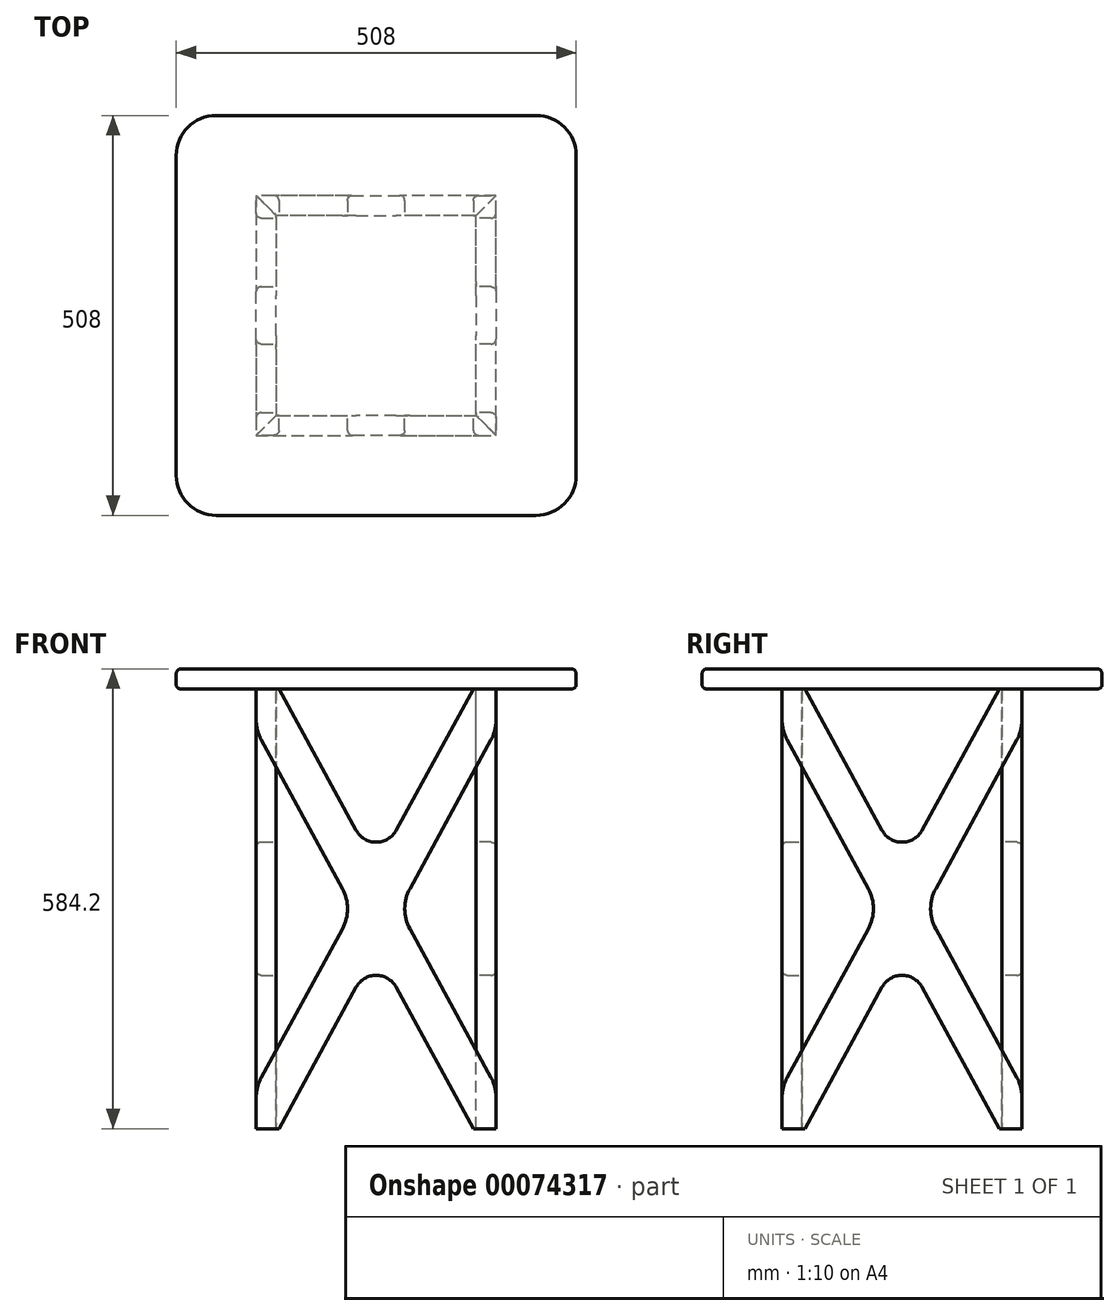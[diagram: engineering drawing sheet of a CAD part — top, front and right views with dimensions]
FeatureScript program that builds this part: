
annotation { "Feature Type Name" : "Feature", "Feature Type Description" : "" }
export const myFeature = defineFeature(function(context is Context, id is Id, definition is map)
    precondition{}
    {
        {
            var Q0;
            Q0=qCreatedBy(makeId("Right.planeOp"),FACE);
            var sketch = newSketch(context, id + "F0", { "sketchPlane" : qUnion([Q0])});
            skLineSegment(sketch, "E0.bottom", {"start": v(-152.4, 558.8) * mm, "end": v(152.4, 558.8) * mm, "construction": true});
            skLineSegment(sketch, "E0.top", {"start": v(-152.4, 0) * mm, "end": v(152.4, 0) * mm, "construction": true});
            skLineSegment(sketch, "E0.left", {"start": v(-152.4, 558.8) * mm, "end": v(-152.4, 505.76) * mm});
            skLineSegment(sketch, "E0.right", {"start": v(152.4, 558.8) * mm, "end": v(152.4, 505.76) * mm});
            skLineSegment(sketch, "E1", {"start": v(-152.4, 0) * mm, "end": v(152.4, 558.8) * mm, "construction": true});
            skLineSegment(sketch, "E2", {"start": v(-152.4, 558.8) * mm, "end": v(152.4, 0) * mm, "construction": true});
            skLineSegment(sketch, "E3.0", {"start": v(-152.4, 505.76) * mm, "end": v(-42.79, 304.8) * mm});
            skLineSegment(sketch, "E4.0", {"start": v(-123.47, 558.8) * mm, "end": v(-25.4, 379.01) * mm});
            skLineSegment(sketch, "E5.0", {"start": v(-123.47, 0) * mm, "end": v(-25.4, 179.79) * mm});
            skLineSegment(sketch, "E6.0", {"start": v(-152.4, 53.04) * mm, "end": v(-42.79, 254) * mm});
            skLineSegment(sketch, "E7.trimOffspring", {"start": v(25.4, 379.01) * mm, "end": v(123.47, 558.8) * mm});
            skLineSegment(sketch, "E8.trimOffspring", {"start": v(25.4, 179.79) * mm, "end": v(123.47, 0) * mm});
            skLineSegment(sketch, "E9.trimOffspring", {"start": v(42.79, 254) * mm, "end": v(152.4, 53.04) * mm});
            skPoint(sketch, "E10.visualSharp", {"position": v(0, 332.44) * mm});
            skArc(sketch, "E10.filletArc", {"start": v(-25.4, 379.01) * mm, "mid": v(0, 363.93) * mm, "end": v(25.4, 379.01) * mm});
            skPoint(sketch, "E11.visualSharp", {"position": v(-28.93, 279.4) * mm});
            skArc(sketch, "E11.filletArc", {"start": v(-42.79, 254) * mm, "mid": v(-36.31, 279.4) * mm, "end": v(-42.79, 304.8) * mm});
            skLineSegment(sketch, "E12.trimOffspring", {"start": v(42.79, 304.8) * mm, "end": v(152.4, 505.76) * mm});
            skPoint(sketch, "E13.visualSharp", {"position": v(0, 226.36) * mm});
            skArc(sketch, "E13.filletArc", {"start": v(25.4, 179.79) * mm, "mid": v(0, 194.87) * mm, "end": v(-25.4, 179.79) * mm});
            skPoint(sketch, "E14.visualSharp", {"position": v(28.93, 279.4) * mm});
            skArc(sketch, "E14.filletArc", {"start": v(42.79, 304.8) * mm, "mid": v(36.31, 279.4) * mm, "end": v(42.79, 254) * mm});
            skLineSegment(sketch, "E15", {"start": v(-123.47, 558.8) * mm, "end": v(-152.4, 558.8) * mm});
            skLineSegment(sketch, "E16", {"start": v(123.47, 558.8) * mm, "end": v(152.4, 558.8) * mm});
            skLineSegment(sketch, "E17", {"start": v(-152.4, 0) * mm, "end": v(-123.47, 0) * mm});
            skLineSegment(sketch, "E18.trimOffspring", {"start": v(123.47, 0) * mm, "end": v(152.4, 0) * mm});
            skLineSegment(sketch, "E19", {"start": v(0, 0) * mm, "end": v(0, 558.8) * mm, "construction": true});
            skPoint(sketch, "E20", {"position": v(0, 279.4) * mm});
            skLineSegment(sketch, "E21.trimOffspring", {"start": v(-152.4, 53.04) * mm, "end": v(-152.4, 0) * mm});
            skLineSegment(sketch, "E22.trimOffspring", {"start": v(152.4, 53.04) * mm, "end": v(152.4, 0) * mm});
            skSolve(sketch);
        }
        {
            var Q0;
            Q0=makeQuery(id+"F0.imprint","IMPRINT",FACE,{"disambiguationData":[TD([[makeQuery(id+"F0.imprint","IMPRINT",EDGE,{"derivedFrom":sQuery(id+"F0.wireOp",EDGE,"E3.0")}),1.0]])]});
            extrude(context, id + "F1", {"entities" : qUnion([Q0]), "depth" : 152.4 * mm, "offsetDistance" : 25.4 * mm, "hasSecondDirection" : true, "secondDirectionOppositeDirection" : false, "secondDirectionDepth" : 127 * mm});
        }
        {
            var Q0;
            Q0=makeQuery(id+"F1.opExtrude","CAP_EDGE",EDGE,{"disambiguationData":[OSD([sQuery(id+"F0.wireOp",EDGE,"E0.right")])],"isStart":true});
            var Q1;
            Q1=makeQuery(id+"F1.opExtrude","CAP_EDGE",EDGE,{"disambiguationData":[OSD([sQuery(id+"F0.wireOp",EDGE,"E22.trimOffspring")])],"isStart":true});
            var Q2;
            Q2=makeQuery(id+"F1.opExtrude","CAP_EDGE",EDGE,{"disambiguationData":[OSD([sQuery(id+"F0.wireOp",EDGE,"E0.left")])],"isStart":true});
            var Q3;
            Q3=makeQuery(id+"F1.opExtrude","CAP_EDGE",EDGE,{"disambiguationData":[OSD([sQuery(id+"F0.wireOp",EDGE,"E21.trimOffspring")])],"isStart":true});
            chamfer(context, id + "F2", {"entities" : qUnion([Q0, Q1, Q2, Q3]), "width" : 25.4 * mm, "tangentPropagation" : true});
        }
        {
            var Q0;
            Q0=makeQuery(id+"F1.opExtrude","CAP_EDGE",EDGE,{"disambiguationData":[OSD([sQuery(id+"F0.wireOp",EDGE,"E3.0")])],"isStart":false});
            var Q1;
            Q1=makeQuery(id+"F1.opExtrude","CAP_EDGE",EDGE,{"disambiguationData":[OSD([sQuery(id+"F0.wireOp",EDGE,"E4.0")])],"isStart":false});
            var Q2;
            Q2=makeQuery(id+"F1.opExtrude","CAP_EDGE",EDGE,{"disambiguationData":[OSD([sQuery(id+"F0.wireOp",EDGE,"E12.trimOffspring")])],"isStart":false});
            var Q3;
            Q3=makeQuery(id+"F1.opExtrude","CAP_EDGE",EDGE,{"disambiguationData":[OSD([sQuery(id+"F0.wireOp",EDGE,"E8.trimOffspring")])],"isStart":false});
            fillet(context, id + "F3", {"entities" : qUnion([Q0, Q1, Q2, Q3]), "tangentPropagation" : true, "radius" : 6.35 * mm, "defaultsChanged" : true, "vertexSettings" : [], "allowEdgeOverflow" : false});
        }
        {
            var Q0;
            Q0=makeQuery(id+"F1.opExtrude","SWEPT_BODY",BODY,{"disambiguationData":[OSD([sQuery(id+"F0.wireOp",EDGE,"E3.0"),sQuery(id+"F0.wireOp",EDGE,"E4.0"),sQuery(id+"F0.wireOp",EDGE,"E5.0"),sQuery(id+"F0.wireOp",EDGE,"E6.0"),sQuery(id+"F0.wireOp",EDGE,"E7.trimOffspring"),sQuery(id+"F0.wireOp",EDGE,"E8.trimOffspring"),sQuery(id+"F0.wireOp",EDGE,"E9.trimOffspring"),sQuery(id+"F0.wireOp",EDGE,"E10.filletArc"),sQuery(id+"F0.wireOp",EDGE,"E11.filletArc"),sQuery(id+"F0.wireOp",EDGE,"E12.trimOffspring"),sQuery(id+"F0.wireOp",EDGE,"E13.filletArc"),sQuery(id+"F0.wireOp",EDGE,"E14.filletArc"),sQuery(id+"F0.wireOp",EDGE,"E15"),sQuery(id+"F0.wireOp",EDGE,"E16"),sQuery(id+"F0.wireOp",EDGE,"E17"),sQuery(id+"F0.wireOp",EDGE,"E18.trimOffspring")])]});
            var Q1;
            Q1=sQuery(id+"F0.wireOp",EDGE,"E19");
            circularPattern(context, id + "F4", {"entities" : qUnion([Q0]), "axis" : qUnion([Q1]), "angle" : 360 * degree, "instanceCount" : 4, "equalSpace" : true});
        }
        {
            var Q0;
            Q0=makeQuery(id+"F1.opExtrude","SWEPT_FACE",FACE,{"disambiguationData":[OSD([sQuery(id+"F0.wireOp",EDGE,"E16")])]});
            var sketch = newSketch(context, id + "F5", { "sketchPlane" : qUnion([Q0])});
            skLineSegment(sketch, "E23.bottom", {"start": v(254, -254) * mm, "end": v(-254, -254) * mm});
            skLineSegment(sketch, "E23.top", {"start": v(254, 254) * mm, "end": v(-254, 254) * mm});
            skLineSegment(sketch, "E23.left", {"start": v(254, -254) * mm, "end": v(254, 254) * mm});
            skLineSegment(sketch, "E23.right", {"start": v(-254, -254) * mm, "end": v(-254, 254) * mm});
            skCircle(sketch, "E24", {"center": v(0, 0) * mm, "radius": 254 * mm, "construction": true});
            skSolve(sketch);
        }
        {
            var Q0;
            Q0=makeQuery(id+"F5.imprint","IMPRINT",FACE,{"disambiguationData":[TD([[makeQuery(id+"F5.imprint","IMPRINT",EDGE,{"derivedFrom":sQuery(id+"F5.wireOp",EDGE,"E23.bottom")}),-1.0]])]});
            var Q1;
            {var subQ0=sQuery(id+"F0.wireOp",EDGE,"E16");Q1=makeQuery(id+"F5.imprint","IMPRINT",FACE,{"disambiguationData":[TD([[makeQuery(id+"F5.imprint","IMPRINT",EDGE,{"derivedFrom":makeQuery(id+"F1.opExtrude","CAP_EDGE",EDGE,{"disambiguationData":[OSD([subQ0])],"isStart":true})}),-1.0]])]});}
            extrude(context, id + "F6", {"entities" : qUnion([Q0, Q1]), "depth" : 25.4 * mm, "offsetDistance" : 25.4 * mm});
        }
        {
            var Q0;
            Q0=makeQuery(id+"F6.opExtrude","SWEPT_EDGE",EDGE,{"disambiguationData":[OSD([sQuery(id+"F5.wireOp",EDGE,"E23.top"),sQuery(id+"F5.wireOp",EDGE,"E23.right")])]});
            var Q1;
            Q1=makeQuery(id+"F6.opExtrude","SWEPT_EDGE",EDGE,{"disambiguationData":[OSD([sQuery(id+"F5.wireOp",EDGE,"E23.bottom"),sQuery(id+"F5.wireOp",EDGE,"E23.right")])]});
            var Q2;
            Q2=makeQuery(id+"F6.opExtrude","SWEPT_EDGE",EDGE,{"disambiguationData":[OSD([sQuery(id+"F5.wireOp",EDGE,"E23.top"),sQuery(id+"F5.wireOp",EDGE,"E23.left")])]});
            var Q3;
            Q3=makeQuery(id+"F6.opExtrude","SWEPT_EDGE",EDGE,{"disambiguationData":[OSD([sQuery(id+"F5.wireOp",EDGE,"E23.bottom"),sQuery(id+"F5.wireOp",EDGE,"E23.left")])]});
            fillet(context, id + "F7", {"entities" : qUnion([Q0, Q1, Q2, Q3]), "tangentPropagation" : true, "radius" : 50.8 * mm, "defaultsChanged" : true, "vertexSettings" : [], "allowEdgeOverflow" : false});
        }
        {
            var Q0;
            Q0=makeQuery(id+"F6.opExtrude","CAP_EDGE",EDGE,{"disambiguationData":[OSD([sQuery(id+"F5.wireOp",EDGE,"E23.bottom")])],"isStart":false});
            fillet(context, id + "F8", {"entities" : qUnion([Q0]), "tangentPropagation" : true, "radius" : 6.35 * mm, "defaultsChanged" : true, "vertexSettings" : [], "allowEdgeOverflow" : false});
        }
        {
            var Q0;
            Q0=makeQuery(id+"F6.opExtrude","CAP_EDGE",EDGE,{"disambiguationData":[OSD([sQuery(id+"F5.wireOp",EDGE,"E23.bottom")])],"isStart":true});
            fillet(context, id + "F9", {"entities" : qUnion([Q0]), "tangentPropagation" : true, "radius" : 5.08 * mm, "defaultsChanged" : false, "vertexSettings" : [], "allowEdgeOverflow" : false});
        }
    });
